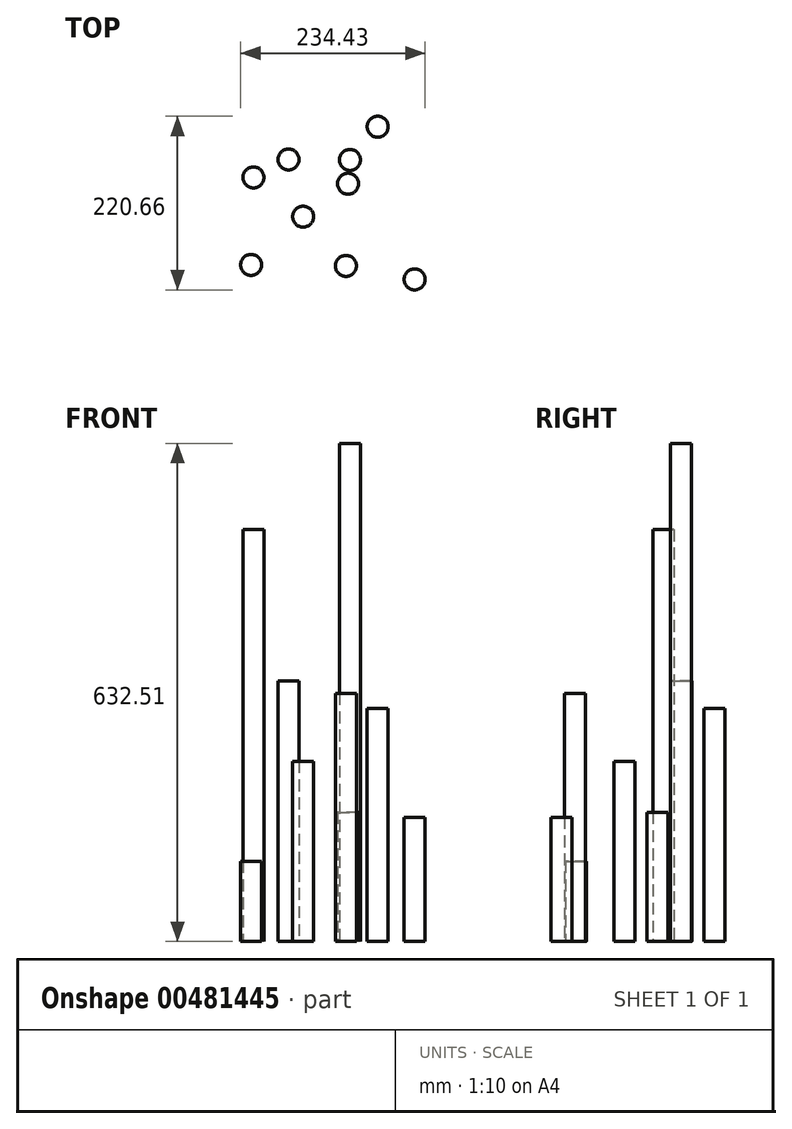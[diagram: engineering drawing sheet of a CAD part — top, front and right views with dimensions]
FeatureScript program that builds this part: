
annotation { "Feature Type Name" : "Feature", "Feature Type Description" : "" }
export const myFeature = defineFeature(function(context is Context, id is Id, definition is map)
    precondition{}
    {
        {
            var Q0;
            Q0=qCreatedBy(makeId("Top.planeOp"),FACE);
            var sketch = newSketch(context, id + "F0", { "sketchPlane" : qUnion([Q0])});
            skCircle(sketch, "E0", {"center": v(0, 0) * mm, "radius": 13.34 * mm});
            skSolve(sketch);
        }
        {
            var Q0;
            Q0=makeQuery(id+"F0.imprint","IMPRINT",FACE,{"disambiguationData":[TD([[makeQuery(id+"F0.imprint","IMPRINT",EDGE,{"derivedFrom":sQuery(id+"F0.wireOp",EDGE,"E0")}),1.0]])]});
            extrude(context, id + "F1", {"entities" : qUnion([Q0]), "depth" : 228.6 * mm});
        }
        {
            var Q0;
            Q0=qCreatedBy(makeId("Top.planeOp"),FACE);
            var sketch = newSketch(context, id + "F2", { "sketchPlane" : qUnion([Q0])});
            skCircle(sketch, "E1", {"center": v(-66.08, -61.29) * mm, "radius": 13.34 * mm});
            skSolve(sketch);
        }
        {
            var Q0;
            Q0=makeQuery(id+"F2.imprint","IMPRINT",FACE,{"disambiguationData":[TD([[makeQuery(id+"F2.imprint","IMPRINT",EDGE,{"derivedFrom":sQuery(id+"F2.wireOp",EDGE,"E1")}),1.0]])]});
            extrude(context, id + "F3", {"entities" : qUnion([Q0]), "depth" : 101.6 * mm});
        }
        {
            var Q0;
            Q0=qCreatedBy(makeId("Top.planeOp"),FACE);
            var sketch = newSketch(context, id + "F4", { "sketchPlane" : qUnion([Q0])});
            skCircle(sketch, "E2", {"center": v(54.35, -62.55) * mm, "radius": 13.34 * mm});
            skSolve(sketch);
        }
        {
            var Q0;
            Q0=makeQuery(id+"F4.imprint","IMPRINT",FACE,{"disambiguationData":[TD([[makeQuery(id+"F4.imprint","IMPRINT",EDGE,{"derivedFrom":sQuery(id+"F4.wireOp",EDGE,"E2")}),1.0]])]});
            extrude(context, id + "F5", {"entities" : qUnion([Q0]), "depth" : 315 * mm});
        }
        {
            var Q0;
            Q0=qCreatedBy(makeId("Top.planeOp"),FACE);
            var sketch = newSketch(context, id + "F6", { "sketchPlane" : qUnion([Q0])});
            skCircle(sketch, "E3", {"center": v(-63.06, 49.8) * mm, "radius": 13.34 * mm});
            skSolve(sketch);
        }
        {
            var Q0;
            Q0 = qSketchRegion(id + "F6", true);
            extrude(context, id + "F7", {"entities" : qUnion([Q0]), "depth" : 523.2 * mm});
        }
        {
            var Q0;
            Q0=qCreatedBy(makeId("Top.planeOp"),FACE);
            var sketch = newSketch(context, id + "F8", { "sketchPlane" : qUnion([Q0])});
            skCircle(sketch, "E4", {"center": v(57.07, 41.86) * mm, "radius": 13.34 * mm});
            skSolve(sketch);
        }
        {
            var Q0;
            Q0=makeQuery(id+"F8.imprint","IMPRINT",FACE,{"disambiguationData":[TD([[makeQuery(id+"F8.imprint","IMPRINT",EDGE,{"derivedFrom":sQuery(id+"F8.wireOp",EDGE,"E4")}),1.0]])]});
            extrude(context, id + "F9", {"entities" : qUnion([Q0]), "depth" : 164.03 * mm});
        }
        {
            var Q0;
            Q0=qCreatedBy(makeId("Top.planeOp"),FACE);
            var sketch = newSketch(context, id + "F10", { "sketchPlane" : qUnion([Q0])});
            skCircle(sketch, "E5", {"center": v(94.75, 114.27) * mm, "radius": 13.34 * mm});
            skSolve(sketch);
        }
        {
            var Q0;
            Q0 = qSketchRegion(id + "F10", true);
            extrude(context, id + "F11", {"entities" : qUnion([Q0]), "depth" : 296 * mm});
        }
        {
            var Q0;
            Q0=qCreatedBy(makeId("Top.planeOp"),FACE);
            var sketch = newSketch(context, id + "F12", { "sketchPlane" : qUnion([Q0])});
            skCircle(sketch, "E6", {"center": v(59.5, 72.07) * mm, "radius": 13.34 * mm});
            skSolve(sketch);
        }
        {
            var Q0;
            Q0 = qSketchRegion(id + "F12", true);
            extrude(context, id + "F13", {"entities" : qUnion([Q0]), "depth" : 632.5 * mm});
        }
        {
            var Q0;
            Q0=qCreatedBy(makeId("Top.planeOp"),FACE);
            var sketch = newSketch(context, id + "F14", { "sketchPlane" : qUnion([Q0])});
            skCircle(sketch, "E7", {"center": v(-18.56, 72.59) * mm, "radius": 13.34 * mm});
            skSolve(sketch);
        }
        {
            var Q0;
            Q0=makeQuery(id+"F14.imprint","IMPRINT",FACE,{"disambiguationData":[TD([[makeQuery(id+"F14.imprint","IMPRINT",EDGE,{"derivedFrom":sQuery(id+"F14.wireOp",EDGE,"E7")}),1.0]])]});
            extrude(context, id + "F15", {"entities" : qUnion([Q0]), "depth" : 330.68 * mm});
        }
        {
            var Q0;
            Q0=qCreatedBy(makeId("Top.planeOp"),FACE);
            var sketch = newSketch(context, id + "F16", { "sketchPlane" : qUnion([Q0])});
            skCircle(sketch, "E8", {"center": v(141.68, -79.72) * mm, "radius": 13.34 * mm});
            skSolve(sketch);
        }
        {
            var Q0;
            Q0=makeQuery(id+"F16.imprint","IMPRINT",FACE,{"disambiguationData":[TD([[makeQuery(id+"F16.imprint","IMPRINT",EDGE,{"derivedFrom":sQuery(id+"F16.wireOp",EDGE,"E8")}),1.0]])]});
            extrude(context, id + "F17", {"entities" : qUnion([Q0]), "depth" : 157.6 * mm});
        }
    });
